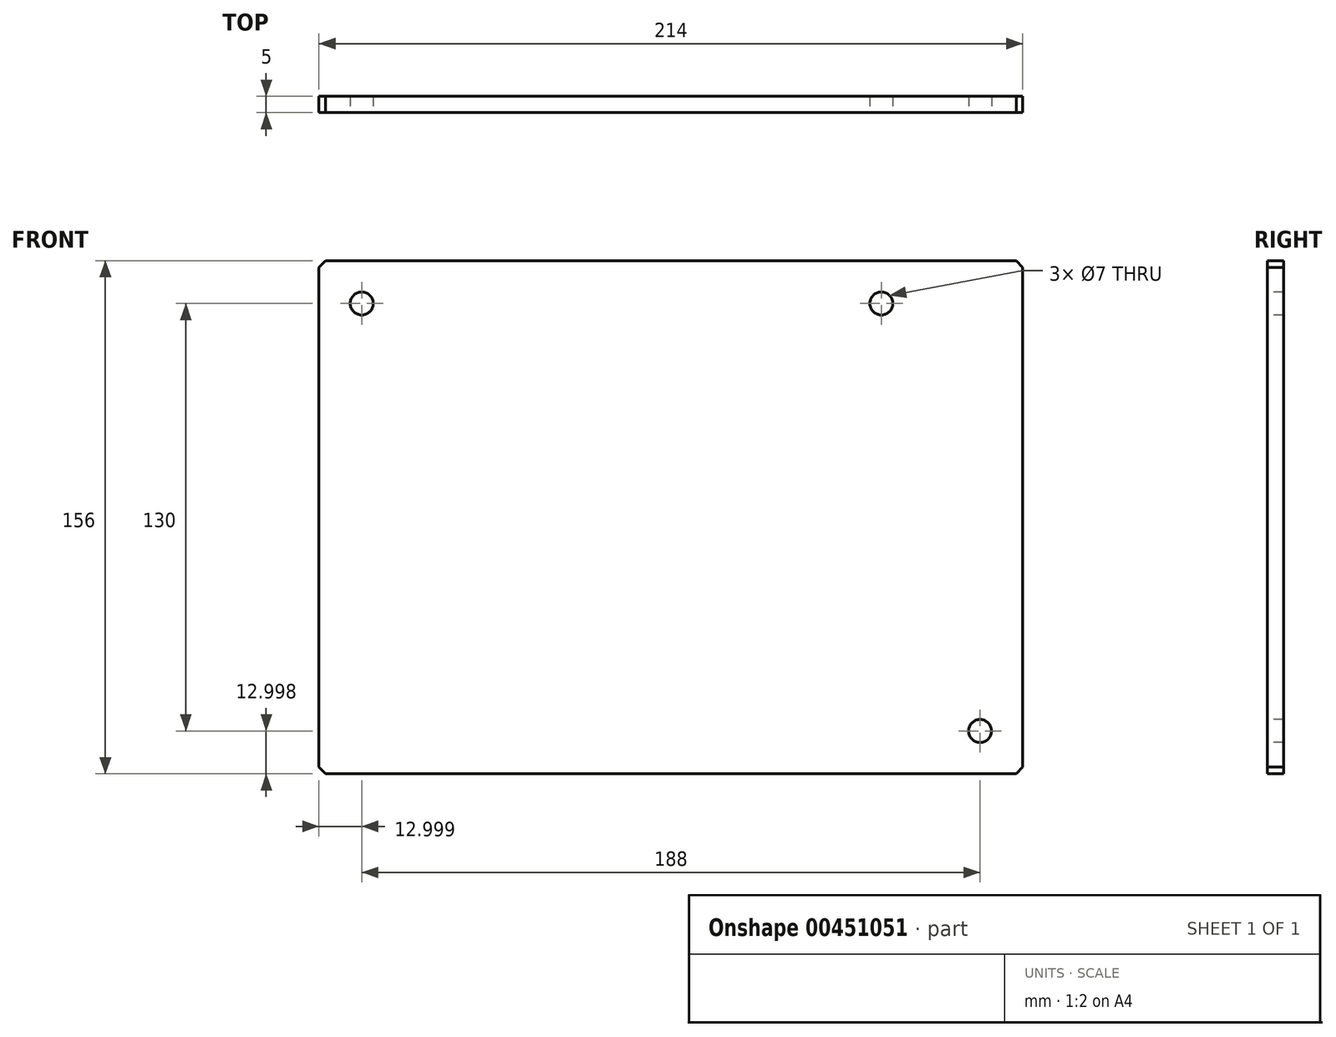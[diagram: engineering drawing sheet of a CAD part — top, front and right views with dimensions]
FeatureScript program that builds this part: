
annotation { "Feature Type Name" : "Feature", "Feature Type Description" : "" }
export const myFeature = defineFeature(function(context is Context, id is Id, definition is map)
    precondition{}
    {
        {
            var Q0;
            Q0=qCreatedBy(makeId("Front.planeOp"),FACE);
            var sketch = newSketch(context, id + "F0", { "sketchPlane" : qUnion([Q0])});
            skLineSegment(sketch, "E0", {"start": v(-338.77, -208.64) * mm, "end": v(201.23, -208.64) * mm});
            skLineSegment(sketch, "E1", {"start": v(-338.77, -154.64) * mm, "end": v(-338.77, -208.64) * mm});
            skLineSegment(sketch, "E2", {"start": v(-338.77, -154.64) * mm, "end": v(201.23, -154.64) * mm});
            skLineSegment(sketch, "E3", {"start": v(-148.77, -200.64) * mm, "end": v(-34.77, -200.64) * mm});
            skLineSegment(sketch, "E4", {"start": v(-148.77, -182.02) * mm, "end": v(-34.77, -182.02) * mm});
            skLineSegment(sketch, "E5", {"start": v(-338.77, -192.64) * mm, "end": v(-148.77, -192.64) * mm});
            skLineSegment(sketch, "E6", {"start": v(-148.77, -154.64) * mm, "end": v(-148.77, -208.64) * mm});
            skLineSegment(sketch, "E7", {"start": v(-70.77, -182.02) * mm, "end": v(-70.77, -208.64) * mm});
            skLineSegment(sketch, "E8", {"start": v(-34.77, -190.64) * mm, "end": v(201.23, -190.64) * mm});
            skLineSegment(sketch, "E9", {"start": v(55.23, -172.64) * mm, "end": v(201.23, -172.64) * mm});
            skLineSegment(sketch, "E10", {"start": v(-34.77, -164.64) * mm, "end": v(55.23, -164.64) * mm});
            skLineSegment(sketch, "E11", {"start": v(50.84, -169.46) * mm, "end": v(35.98, -187.55) * mm});
            skLineSegment(sketch, "E12", {"start": v(-34.77, -154.64) * mm, "end": v(-34.77, -208.64) * mm});
            skLineSegment(sketch, "E13", {"start": v(-0.77, -154.64) * mm, "end": v(-0.77, -190.64) * mm});
            skLineSegment(sketch, "E14", {"start": v(-32.89, -177.68) * mm, "end": v(-17.44, -177.68) * mm});
            skCircle(sketch, "E15", {"center": v(-25.16, -177.68) * mm, "radius": 5.94 * mm});
            skCircle(sketch, "E16", {"center": v(-25.16, -177.68) * mm, "radius": 2.93 * mm});
            skLineSegment(sketch, "E17", {"start": v(-25.16, -169.96) * mm, "end": v(-25.16, -185.4) * mm});
            skLineSegment(sketch, "E18", {"start": v(-5.25, -171.74) * mm, "end": v(-5.25, -183.63) * mm});
            skLineSegment(sketch, "E19", {"start": v(-13.42, -174.75) * mm, "end": v(-13.42, -180.62) * mm});
            skLineSegment(sketch, "E20", {"start": v(-5.25, -183.63) * mm, "end": v(-13.42, -180.62) * mm});
            skLineSegment(sketch, "E21", {"start": v(-15.06, -177.68) * mm, "end": v(-3.39, -177.68) * mm});
            skLineSegment(sketch, "E22", {"start": v(-5.25, -171.74) * mm, "end": v(-13.42, -174.75) * mm});
            skLineSegment(sketch, "E23", {"start": v(33.23, -154.64) * mm, "end": v(33.23, -190.64) * mm});
            skLineSegment(sketch, "E24", {"start": v(55.23, -154.64) * mm, "end": v(55.23, -190.64) * mm});
            skLineSegment(sketch, "E25", {"start": v(145.23, -190.64) * mm, "end": v(145.23, -208.64) * mm});
            skLineSegment(sketch, "E26", {"start": v(145.23, -154.64) * mm, "end": v(145.23, -172.64) * mm});
            skLineSegment(sketch, "E27", {"start": v(201.23, 159.36) * mm, "end": v(5.23, 159.36) * mm});
            skLineSegment(sketch, "E28", {"start": v(201.23, 147.36) * mm, "end": v(5.23, 147.36) * mm});
            skLineSegment(sketch, "E29", {"start": v(201.23, 135.36) * mm, "end": v(5.23, 135.36) * mm});
            skLineSegment(sketch, "E30", {"start": v(33.23, 171.36) * mm, "end": v(33.23, 135.36) * mm});
            skLineSegment(sketch, "E31", {"start": v(5.23, 171.36) * mm, "end": v(5.23, 135.36) * mm});
            skLineSegment(sketch, "E32", {"start": v(14.07, 161.56) * mm, "end": v(23.67, 161.56) * mm});
            skLineSegment(sketch, "E33", {"start": v(151.23, 171.36) * mm, "end": v(151.23, 135.36) * mm});
            skLineSegment(sketch, "E34", {"start": v(181.23, 171.36) * mm, "end": v(181.23, 135.36) * mm});
            skLineSegment(sketch, "E35", {"start": v(14.07, 161.56) * mm, "end": v(18.87, 169.56) * mm});
            skLineSegment(sketch, "E36", {"start": v(18.87, 169.56) * mm, "end": v(23.67, 161.56) * mm});
            skLineSegment(sketch, "E37", {"start": v(14.07, 149.56) * mm, "end": v(23.67, 149.56) * mm});
            skLineSegment(sketch, "E38", {"start": v(14.07, 149.56) * mm, "end": v(18.87, 157.56) * mm});
            skLineSegment(sketch, "E39", {"start": v(18.87, 157.56) * mm, "end": v(23.67, 149.56) * mm});
            skLineSegment(sketch, "E40", {"start": v(-338.77, -208.64) * mm, "end": v(-338.77, 171.36) * mm});
            skLineSegment(sketch, "E41", {"start": v(201.23, -208.64) * mm, "end": v(201.23, 171.36) * mm});
            skLineSegment(sketch, "E42", {"start": v(-338.77, 171.36) * mm, "end": v(201.23, 171.36) * mm});
            skLineSegment(sketch, "E43", {"start": v(-225.76, 65.45) * mm, "end": v(-225.76, -86.55) * mm});
            skLineSegment(sketch, "E44", {"start": v(-223.76, -88.55) * mm, "end": v(-225.76, -86.55) * mm});
            skLineSegment(sketch, "E45", {"start": v(-223.76, 67.45) * mm, "end": v(-225.76, 65.45) * mm});
            skLineSegment(sketch, "E46", {"start": v(-11.76, -86.55) * mm, "end": v(-13.76, -88.55) * mm});
            skLineSegment(sketch, "E47", {"start": v(-11.76, 65.45) * mm, "end": v(-11.76, -86.55) * mm});
            skLineSegment(sketch, "E48", {"start": v(-223.76, 67.45) * mm, "end": v(-13.76, 67.45) * mm});
            skLineSegment(sketch, "E49", {"start": v(-11.76, 65.45) * mm, "end": v(-13.76, 67.45) * mm});
            skLineSegment(sketch, "E50", {"start": v(-13.76, -88.55) * mm, "end": v(-223.76, -88.55) * mm});
            skLineSegment(sketch, "E51", {"start": v(82.6, 67.45) * mm, "end": v(77.6, 67.45) * mm});
            skLineSegment(sketch, "E52", {"start": v(77.6, 67.45) * mm, "end": v(77.6, -88.55) * mm});
            skLineSegment(sketch, "E53", {"start": v(82.6, 67.45) * mm, "end": v(82.6, -88.55) * mm});
            skLineSegment(sketch, "E54", {"start": v(82.6, -88.55) * mm, "end": v(77.6, -88.55) * mm});
            skLineSegment(sketch, "E55", {"start": v(-95.7, -170.46) * mm, "end": v(-92.82, -175.46) * mm});
            skLineSegment(sketch, "E56", {"start": v(-92.82, -175.46) * mm, "end": v(-86.47, -164.46) * mm});
            skCircle(sketch, "E57", {"center": v(-24.76, -75.55) * mm, "radius": 3.5 * mm});
            skLineSegment(sketch, "E58", {"start": v(-29.31, -75.55) * mm, "end": v(-20.21, -75.55) * mm});
            skLineSegment(sketch, "E59", {"start": v(-24.76, -80.1) * mm, "end": v(-24.76, -71) * mm});
            skCircle(sketch, "E60", {"center": v(-54.76, 54.45) * mm, "radius": 3.5 * mm});
            skLineSegment(sketch, "E61", {"start": v(-59.31, 54.45) * mm, "end": v(-50.21, 54.45) * mm});
            skLineSegment(sketch, "E62", {"start": v(-54.76, 49.9) * mm, "end": v(-54.76, 59) * mm});
            skCircle(sketch, "E63", {"center": v(-212.76, 54.45) * mm, "radius": 3.5 * mm});
            skLineSegment(sketch, "E64", {"start": v(-217.31, 54.45) * mm, "end": v(-208.21, 54.45) * mm});
            skLineSegment(sketch, "E65", {"start": v(-212.76, 49.9) * mm, "end": v(-212.76, 59) * mm});
            skSolve(sketch);
        }
        {
            var Q0;
            Q0=makeQuery(id+"F0.imprint","IMPRINT",FACE,{"disambiguationData":[TD([[makeQuery(id+"F0.imprint","IMPRINT",EDGE,{"derivedFrom":sQuery(id+"F0.wireOp",EDGE,"E43")}),1.0]])]});
            extrude(context, id + "F1", {"entities" : qUnion([Q0]), "oppositeDirection" : true, "depth" : 5 * mm});
        }
    });
